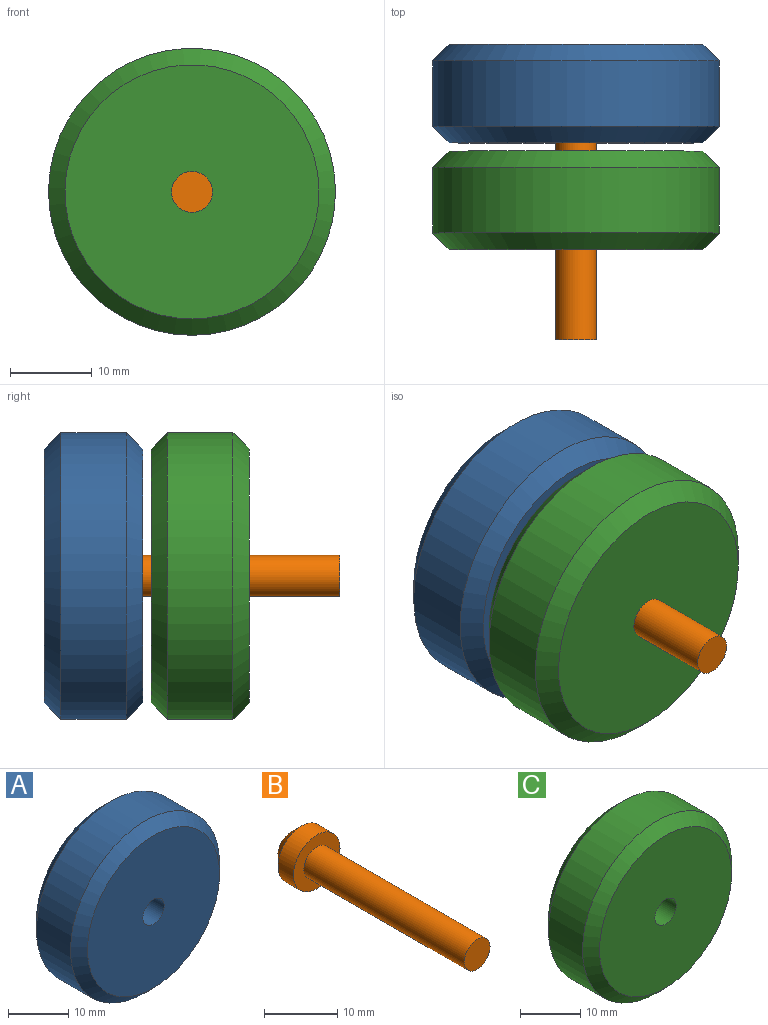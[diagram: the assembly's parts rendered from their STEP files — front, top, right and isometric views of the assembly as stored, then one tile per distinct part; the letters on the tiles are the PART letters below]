
ASSEMBLY  parts=3 mates=4
PART A: 9 faces, bbox 35x12x35 mm
  f0: cylinder r=17.5mm len=35mm, axis (0,1,0), area 879.6mm2, adj f7,f8
  f1: cylinder r=2.5mm len=7mm, axis (0,1,0), area 110mm2, adj f2,f5
  f2: plane 31x31mm, normal (0,-1,0), area 735.1mm2, adj f1,f7
  f3: plane 31x31mm, normal (0,1,0), area 391.7mm2, adj f6,f8
  f4: cylinder r=8.75mm len=17.5mm, axis (0,1,0), area 164.9mm2, adj f5,f6
  f5: plane 17.5x17.5mm, normal (0,1,0), area 220.9mm2, adj f1,f4
  f6: cone r=10.75mm half-angle=45deg, axis (0,1,0), area 173.3mm2, adj f3,f4
  f7: cone r=15.5mm half-angle=45deg, axis (0,1,0), area 293.2mm2, adj f0,f2
  f8: cone r=17.5mm half-angle=45deg, axis (0,-1,0), area 293.2mm2, adj f0,f3
PART B: 6 faces, bbox 9x36x9 mm
  f0: cylinder r=2.5mm len=31mm, axis (0,1,0), area 486.9mm2, adj f1,f3
  f1: plane 5x5mm, normal (0,-1,0), area 19.6mm2, adj f0
  f2: cylinder r=4.5mm len=9mm, axis (0,1,0), area 84.8mm2, adj f3,f5
  f3: plane 9x9mm, normal (0,-1,0), area 44mm2, adj f0,f2
  f4: plane 5x5mm, normal (0,1,0), area 19.6mm2, adj f5
  f5: cone r=4.5mm half-angle=45deg, axis (0,-1,0), area 62.2mm2, adj f2,f4
PART C: 6 faces, bbox 35x12x35 mm
  f0: cylinder r=17.5mm len=35mm, axis (0,1,0), area 879.6mm2, adj f4,f5
  f1: cylinder r=2.5mm len=12mm, axis (0,1,0), area 188.5mm2, adj f2,f3
  f2: plane 31x31mm, normal (0,-1,0), area 735.1mm2, adj f1,f4
  f3: plane 31x31mm, normal (0,1,0), area 735.1mm2, adj f1,f5
  f4: cone r=15.5mm half-angle=45deg, axis (0,1,0), area 293.2mm2, adj f0,f2
  f5: cone r=17.5mm half-angle=45deg, axis (0,-1,0), area 293.2mm2, adj f0,f3
PLACE A rot(axis=(0.88,0.24,-0.41),0deg) t=(78.03,92.1,-67.59)mm
PLACE B rot(axis=(0.88,0.24,-0.41),0deg) t=(78.03,92.1,-67.59)mm
PLACE C rot(axis=(0.88,0.24,-0.41),0deg) t=(78.03,91.6,-67.59)mm
MATE planar C.f0 <-> A.f0  axis (0,1,0) through (161.03,79.1,-67.59)mm
MATE planar A.f0 <-> B.f0  axis (0,1,0) through (161.03,87.1,-67.59)mm
MATE slider C.f0 <-> B.f0  axis (0,1,0) through (161.03,73.1,-67.59)mm
MATE cylindrical A.f0 <-> B.f0  axis (0,1,0) through (161.03,83.6,-67.59)mm
